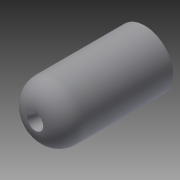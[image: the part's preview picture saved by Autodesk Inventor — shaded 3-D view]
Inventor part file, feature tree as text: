
AUTODESK INVENTOR PART (.ipt)
format: ipt  version: 2015 (Build 190159000, 159)  size: 124,416 bytes
history: native  units: in
note: dims shown in document units (in); Inventor stores cm internally (conversion verified against a paired STEP export)
features: extrude x3, sketch x3, fillet x1, chamfer x1
ambient origin geometry x8: Origin, YZ Plane, XZ Plane, XY Plane, X Axis, Y Axis, Z Axis, Center Point
bodies: Solid1 (feature_tree)
feature tree (8):
  extrude  "Extrusion1"  Depth=0.5in
  extrude  "Extrusion6"  Depth=0.1065in
  fillet  "Fillet2"  Radius=0.1065in
  extrude  "Extrusion7"  Depth=1.5in TaperAngle=0.0deg
  chamfer  "Chamfer1"  Distance=0.3125in
  sketch  "Sketch1"  dims[d0=0.5in d1=0.0in d12=0.2402in]
  sketch  "Sketch7"  dims[d13=0.1065in d14=0.1065in d15=0.1065in]
  sketch  "Sketch8"  dims[d16=0.1065in d17=1.5in d18=0.0in d19=0.3125in d21=0.25in d22=1.5in d23=0.0in d24=0.0625in d25=0.125in d26=45.0deg]
